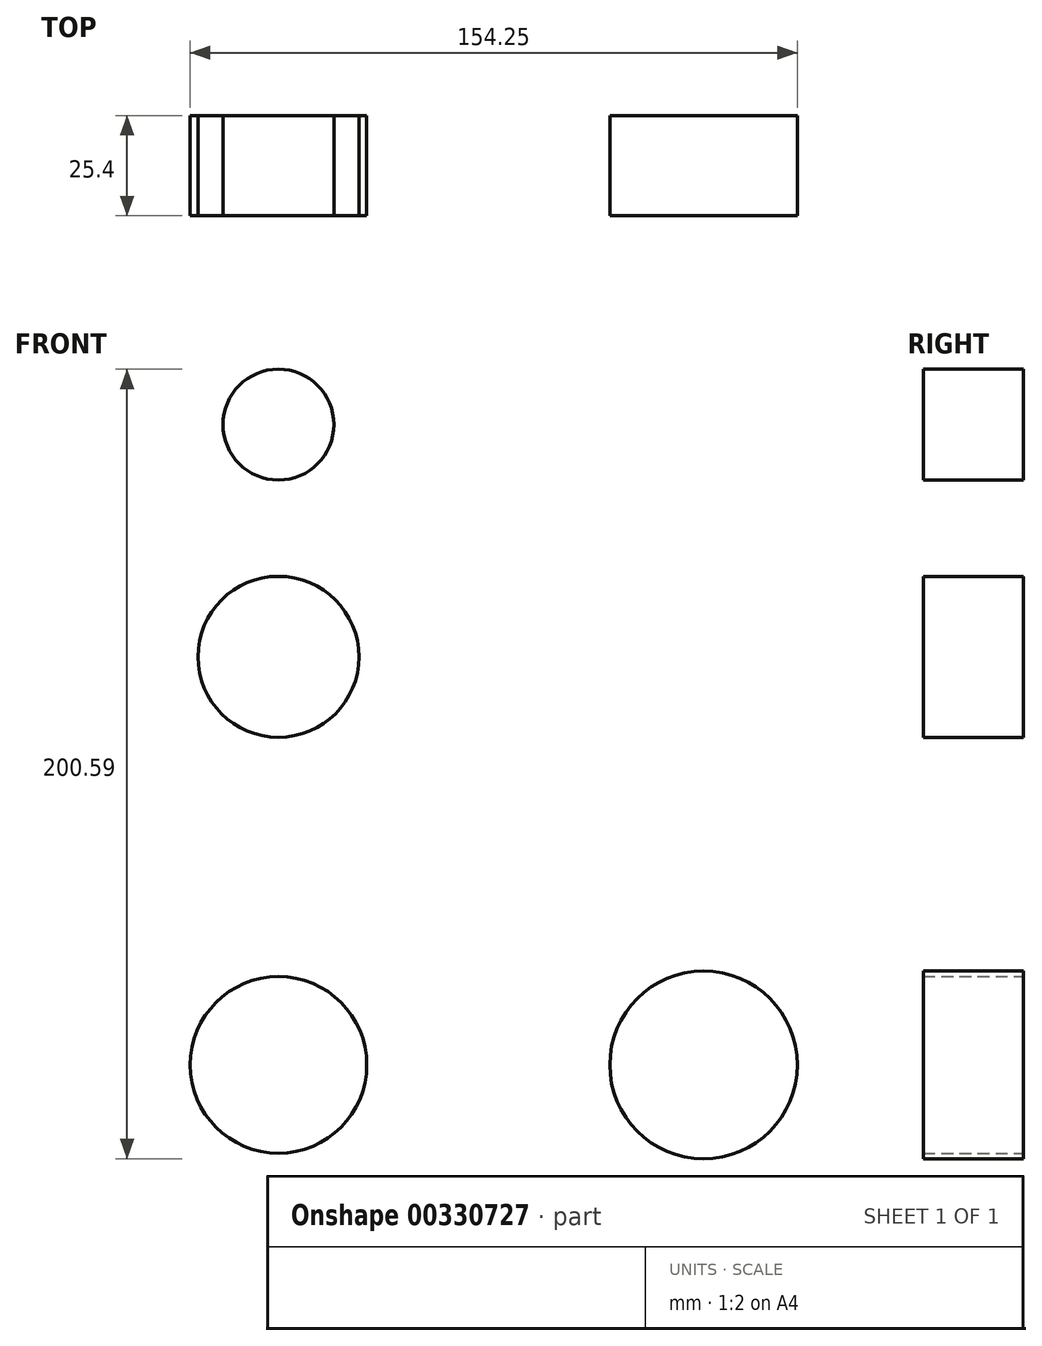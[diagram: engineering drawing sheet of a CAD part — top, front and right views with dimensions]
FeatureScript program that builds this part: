
annotation { "Feature Type Name" : "Feature", "Feature Type Description" : "" }
export const myFeature = defineFeature(function(context is Context, id is Id, definition is map)
    precondition{}
    {
        {
            var Q0;
            Q0=qCreatedBy(makeId("Front.planeOp"),FACE);
            var sketch = newSketch(context, id + "F0", { "sketchPlane" : qUnion([Q0])});
            skLineSegment(sketch, "E0", {"start": v(0, 0) * mm, "end": v(0, 162.67) * mm});
            skLineSegment(sketch, "E1", {"start": v(0, 162.67) * mm, "end": v(0, 0) * mm});
            skLineSegment(sketch, "E2", {"start": v(0, 0) * mm, "end": v(108, 0) * mm});
            skCircle(sketch, "E3", {"center": v(0, 162.67) * mm, "radius": 14.09 * mm});
            skCircle(sketch, "E4", {"center": v(0, 0) * mm, "radius": 22.43 * mm});
            skCircle(sketch, "E5", {"center": v(0, 103.66) * mm, "radius": 20.45 * mm});
            skCircle(sketch, "E6", {"center": v(108, 0) * mm, "radius": 23.83 * mm});
            skSolve(sketch);
        }
        {
            var Q0;
            Q0=qCreatedBy(makeId("Front.planeOp"),FACE);
            var sketch = newSketch(context, id + "F1", { "sketchPlane" : qUnion([Q0])});
            skSolve(sketch);
        }
        {
            var Q0;
            Q0=sQuery(id+"F0.wireOp",EDGE,"E3");
            extrude(context, id + "F2", {"bodyType" : ToolBodyType.SURFACE, "surfaceEntities" : qUnion([Q0]), "depth" : 25.4 * mm});
        }
        {
            var Q0;
            Q0 = qSketchRegion(id + "F0", true);
            var Q1;
            Q1 = qSketchRegion(id + "F1", true);
            extrude(context, id + "F3", {"entities" : qUnion([Q0, Q1]), "depth" : 25.4 * mm});
        }
    });
